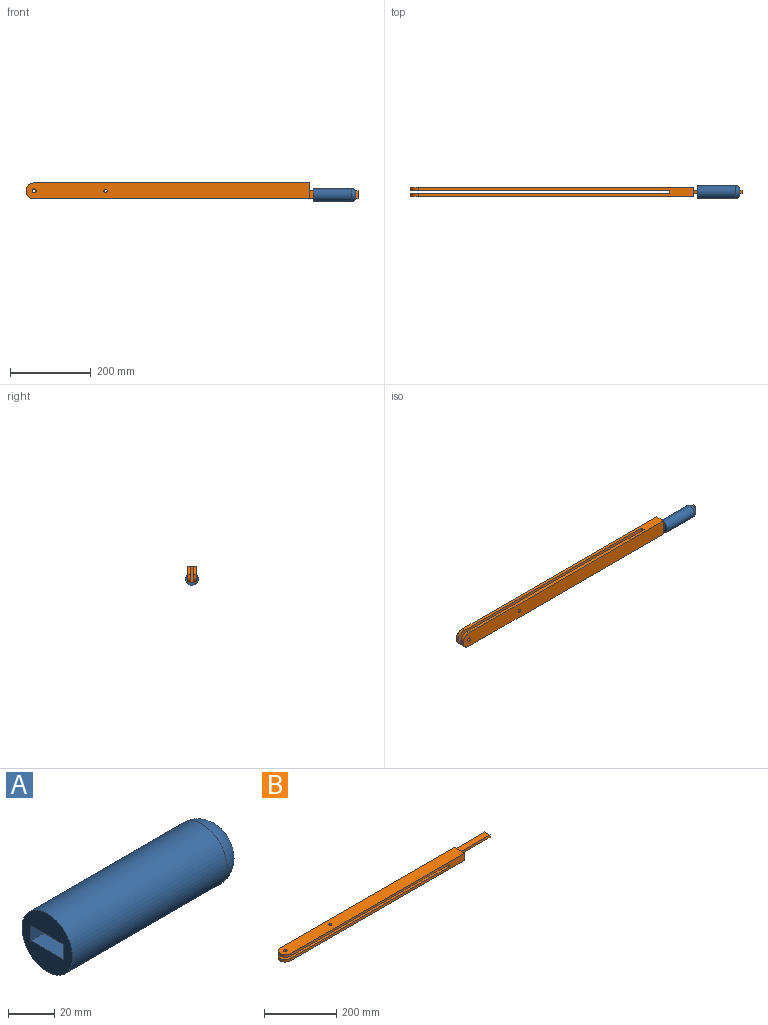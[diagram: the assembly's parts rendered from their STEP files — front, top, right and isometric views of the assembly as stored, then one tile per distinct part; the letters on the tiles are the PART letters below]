
ASSEMBLY  parts=2 mates=1
PART A: 9 faces, bbox 105x31x31 mm
  f0: plane 11x11mm, normal (1,0,0), area 95mm2, adj f8
  f1: plane 31x31mm, normal (-1,0,0), area 594.8mm2, adj f2,f3,f4,f5,f6
  f2: cylinder r=15.5mm len=95mm, axis (-1,0,0), area 9252mm2, adj f1,f8
  f3: plane 100x20mm, normal (0,0,1), area 2000mm2, adj f1,f4,f6,f7
  f4: plane 100x8mm, normal (0,-1,0), area 800mm2, adj f1,f3,f5,f7
  f5: plane 100x20mm, normal (0,0,-1), area 2000mm2, adj f1,f4,f6,f7
  f6: plane 100x8mm, normal (0,1,0), area 800mm2, adj f1,f3,f5,f7
  f7: plane 20x8mm, normal (-1,0,0), area 160mm2, adj f3,f4,f5,f6
  f8: torus R=5.5mm, axis (1,0,0), area 1171.1mm2, adj f0,f2
PART B: 20 faces, bbox 820x40x24 mm
  f0: plane 120x20mm, normal (0,0,1), area 2400mm2, adj f2,f4,f8,f11
  f1: plane 640x40mm, normal (0,0,1), area 25299.5mm2, adj f4,f5,f7,f13,f16,f17,f19
  f2: plane 40x24mm, normal (1,0,0), area 800mm2, adj f0,f3,f4,f5,f6,f9,f11
  f3: plane 700x40mm, normal (0,0,-1), area 27699.5mm2, adj f2,f4,f5,f13,f16,f17,f19
  f4: plane 800x24mm, normal (0,1,0), area 12320mm2, adj f0,f1,f2,f3,f6,f7,f8,f9
  f5: plane 680x24mm, normal (0,-1,0), area 11360mm2, adj f1,f2,f3,f7,f9,f10,f15,f17
  f6: plane 120x20mm, normal (0,0,-1), area 2400mm2, adj f2,f4,f8,f11
  f7: plane 40x8mm, normal (-1,0,0), area 320mm2, adj f1,f4,f5,f10
  f8: plane 20x8mm, normal (1,0,0), area 160mm2, adj f0,f4,f6,f11
  f9: plane 700x40mm, normal (0,0,1), area 27699.5mm2, adj f2,f4,f5,f12,f14,f15,f18
  f10: plane 640x40mm, normal (0,0,-1), area 25299.5mm2, adj f4,f5,f7,f12,f14,f15,f18
  f11: plane 120x8mm, normal (0,-1,0), area 960mm2, adj f0,f2,f6,f8
  f12: cylinder r=5mm len=10mm, axis (0,0,1), area 251.3mm2, adj f9,f10
  f13: cylinder r=5mm len=10mm, axis (0,0,1), area 251.3mm2, adj f1,f3
  f14: cylinder r=20mm len=20mm, axis (0,0,1), area 251.3mm2, adj f4,f9,f10,f15
  f15: cylinder r=20mm len=20mm, axis (0,0,-1), area 251.3mm2, adj f5,f9,f10,f14
  f16: cylinder r=20mm len=20mm, axis (0,0,-1), area 251.3mm2, adj f1,f3,f4,f17
  f17: cylinder r=20mm len=20mm, axis (0,0,1), area 251.3mm2, adj f1,f3,f5,f16
  f18: cylinder r=4mm len=8mm, axis (0,0,1), area 201.1mm2, adj f9,f10
  f19: cylinder r=4mm len=8mm, axis (0,0,1), area 201.1mm2, adj f1,f3
PLACE A rot(axis=(1,0,0),90deg) t=(321.09,-97.27,28.21)mm
PLACE B rot(axis=(-1,0,0),90deg) t=(-83.01,33.97,58.21)mm
MATE fastened A.f5 <-> B.f6  axis (0,1,0) through (371.09,-101.27,28.21)mm
